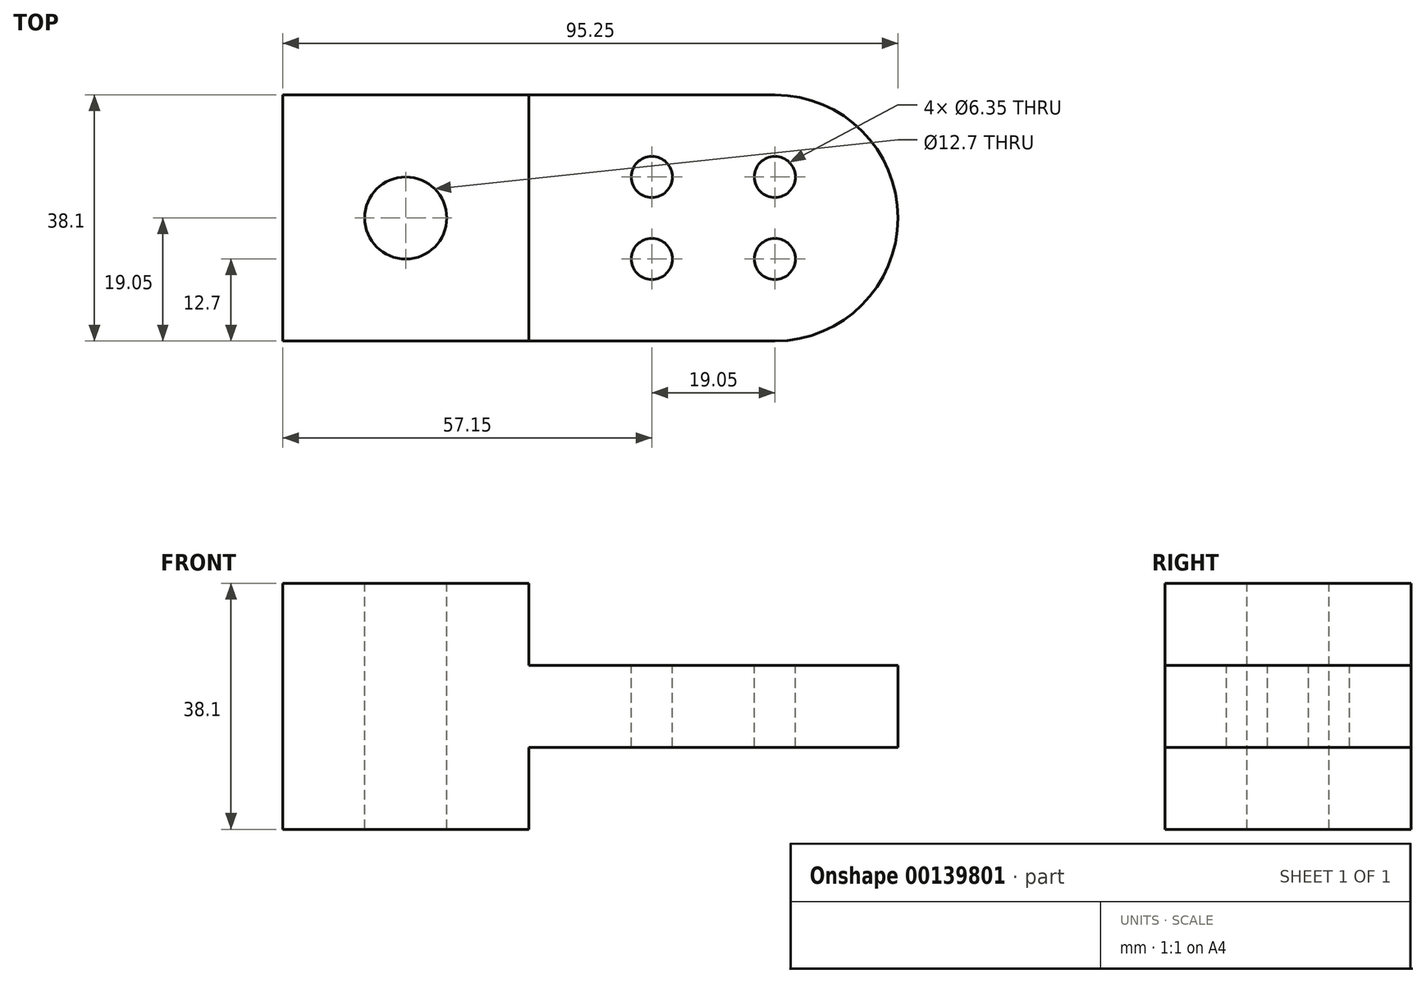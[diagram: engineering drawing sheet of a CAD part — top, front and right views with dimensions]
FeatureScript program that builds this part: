
annotation { "Feature Type Name" : "Feature", "Feature Type Description" : "" }
export const myFeature = defineFeature(function(context is Context, id is Id, definition is map)
    precondition{}
    {
        {
            var Q0;
            Q0=qCreatedBy(makeId("Top.planeOp"),FACE);
            var sketch = newSketch(context, id + "F0", { "sketchPlane" : qUnion([Q0])});
            skLineSegment(sketch, "E0.bottom", {"start": v(0, 0) * mm, "end": v(38.1, 0) * mm});
            skLineSegment(sketch, "E0.top", {"start": v(0, 38.1) * mm, "end": v(38.1, 38.1) * mm});
            skLineSegment(sketch, "E0.left", {"start": v(0, 0) * mm, "end": v(0, 38.1) * mm});
            skLineSegment(sketch, "E0.right", {"start": v(38.1, 0) * mm, "end": v(38.1, 38.1) * mm});
            skLineSegment(sketch, "E1.bottom", {"start": v(38.1, 38.1) * mm, "end": v(76.2, 38.1) * mm});
            skLineSegment(sketch, "E1.top", {"start": v(38.1, 0) * mm, "end": v(76.2, 0) * mm});
            skLineSegment(sketch, "E1.left", {"start": v(38.1, 38.1) * mm, "end": v(38.1, 0) * mm});
            skArc(sketch, "E2", {"start": v(76.2, 0) * mm, "mid": v(95.25, 19.05) * mm, "end": v(76.2, 38.1) * mm});
            skSolve(sketch);
        }
        {
            var Q0;
            Q0=makeQuery(id+"F0.imprint","IMPRINT",FACE,{"disambiguationData":[TD([[makeQuery(id+"F0.imprint","IMPRINT",EDGE,{"derivedFrom":sQuery(id+"F0.wireOp",EDGE,"E0.bottom")}),1.0]])]});
            extrude(context, id + "F1", {"entities" : qUnion([Q0]), "endBound" : BoundingType.SYMMETRIC, "depth" : 38.1 * mm});
        }
        {
            var Q0;
            Q0=makeQuery(id+"F0.imprint","IMPRINT",FACE,{"disambiguationData":[TD([[makeQuery(id+"F0.imprint","IMPRINT",EDGE,{"derivedFrom":sQuery(id+"F0.wireOp",EDGE,"E1.bottom")}),-1.0]])]});
            extrude(context, id + "F2", {"entities" : qUnion([Q0]), "operationType" : NewBodyOperationType.ADD, "endBound" : BoundingType.SYMMETRIC, "depth" : 12.7 * mm});
        }
        {
            var Q0;
            Q0=makeQuery(id+"F1.opExtrude","CAP_FACE",FACE,{"disambiguationData":[OSD([sQuery(id+"F0.wireOp",EDGE,"E0.bottom"),sQuery(id+"F0.wireOp",EDGE,"E0.top"),sQuery(id+"F0.wireOp",EDGE,"E0.left"),sQuery(id+"F0.wireOp",EDGE,"E1.left")])],"isStart":false});
            var sketch = newSketch(context, id + "F3", { "sketchPlane" : qUnion([Q0])});
            skPoint(sketch, "E3", {"position": v(19.05, 19.05) * mm});
            skPoint(sketch, "E3.positionSnap0", {"position": v(0, 19.05) * mm});
            skPoint(sketch, "E3.positionSnap1", {"position": v(19.05, 38.1) * mm});
            skLineSegment(sketch, "E4.bottom", {"start": v(38.1, 38.1) * mm, "end": v(76.2, 38.1) * mm});
            skLineSegment(sketch, "E4.top", {"start": v(38.1, 0) * mm, "end": v(76.2, 0) * mm});
            skLineSegment(sketch, "E4.left", {"start": v(38.1, 38.1) * mm, "end": v(38.1, 0) * mm});
            skLineSegment(sketch, "E4.right", {"start": v(76.2, 38.1) * mm, "end": v(76.2, 0) * mm});
            skPoint(sketch, "E5", {"position": v(76.2, 25.4) * mm});
            skPoint(sketch, "E6", {"position": v(76.2, 12.7) * mm});
            skPoint(sketch, "E7", {"position": v(57.15, 25.4) * mm});
            skPoint(sketch, "E8", {"position": v(57.15, 12.7) * mm});
            skSolve(sketch);
        }
        {
            var Q0;
            Q0=sQuery(id+"F3.wireOp",VERTEX,"E7");
            var Q1;
            Q1=sQuery(id+"F3.wireOp",VERTEX,"E8");
            var Q2;
            Q2=sQuery(id+"F3.wireOp",VERTEX,"E6");
            var Q3;
            Q3=sQuery(id+"F3.wireOp",VERTEX,"E5");
            var Q4;
            Q4=makeQuery(id+"F1.opExtrude","SWEPT_BODY",BODY,{"disambiguationData":[OSD([sQuery(id+"F0.wireOp",EDGE,"E0.bottom"),sQuery(id+"F0.wireOp",EDGE,"E0.top"),sQuery(id+"F0.wireOp",EDGE,"E0.left"),sQuery(id+"F0.wireOp",EDGE,"E1.left")])]});
            hole(context, id + "F4", {"style" : HoleStyle.SIMPLE, "endStyle" : HoleEndStyle.THROUGH, "holeDiameter" : 6.35 * mm, "locations" : qUnion([Q0, Q1, Q2, Q3]), "scope" : qUnion([Q4]), "isTappedThrough" : true});
        }
        {
            var Q0;
            Q0=sQuery(id+"F3.wireOp",VERTEX,"E3");
            var Q1;
            Q1=makeQuery(id+"F1.opExtrude","SWEPT_BODY",BODY,{"disambiguationData":[OSD([sQuery(id+"F0.wireOp",EDGE,"E0.bottom"),sQuery(id+"F0.wireOp",EDGE,"E0.top"),sQuery(id+"F0.wireOp",EDGE,"E0.left"),sQuery(id+"F0.wireOp",EDGE,"E1.left")])]});
            hole(context, id + "F5", {"style" : HoleStyle.SIMPLE, "endStyle" : HoleEndStyle.THROUGH, "holeDiameter" : 12.7 * mm, "locations" : qUnion([Q0]), "scope" : qUnion([Q1]), "isTappedThrough" : true});
        }
    });
